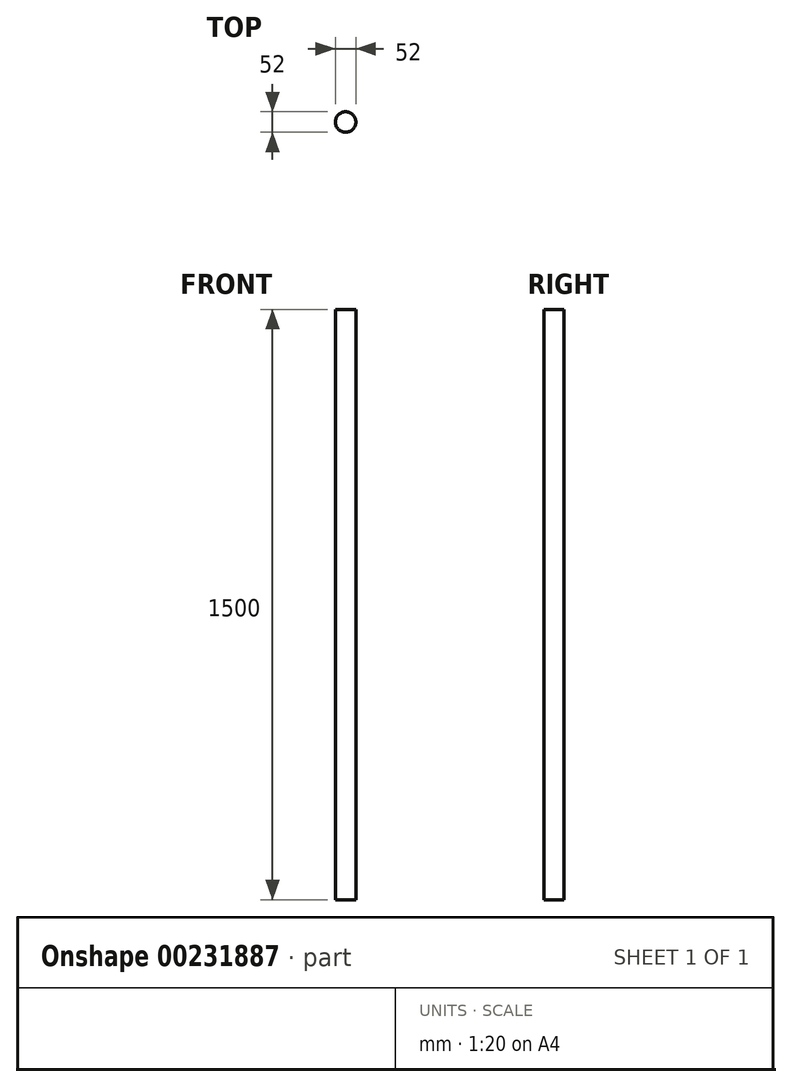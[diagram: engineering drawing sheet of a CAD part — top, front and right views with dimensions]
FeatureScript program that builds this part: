
annotation { "Feature Type Name" : "Feature", "Feature Type Description" : "" }
export const myFeature = defineFeature(function(context is Context, id is Id, definition is map)
    precondition{}
    {
        {
            var Q0;
            Q0=qCreatedBy(makeId("Top.planeOp"),FACE);
            var sketch = newSketch(context, id + "F0", { "sketchPlane" : qUnion([Q0])});
            skCircle(sketch, "E0", {"center": v(0, 0) * mm, "radius": 26 * mm});
            skSolve(sketch);
        }
        {
            var Q0;
            Q0 = qSketchRegion(id + "F0", true);
            extrude(context, id + "F1", {"entities" : qUnion([Q0]), "depth" : 1500 * mm});
        }
    });
